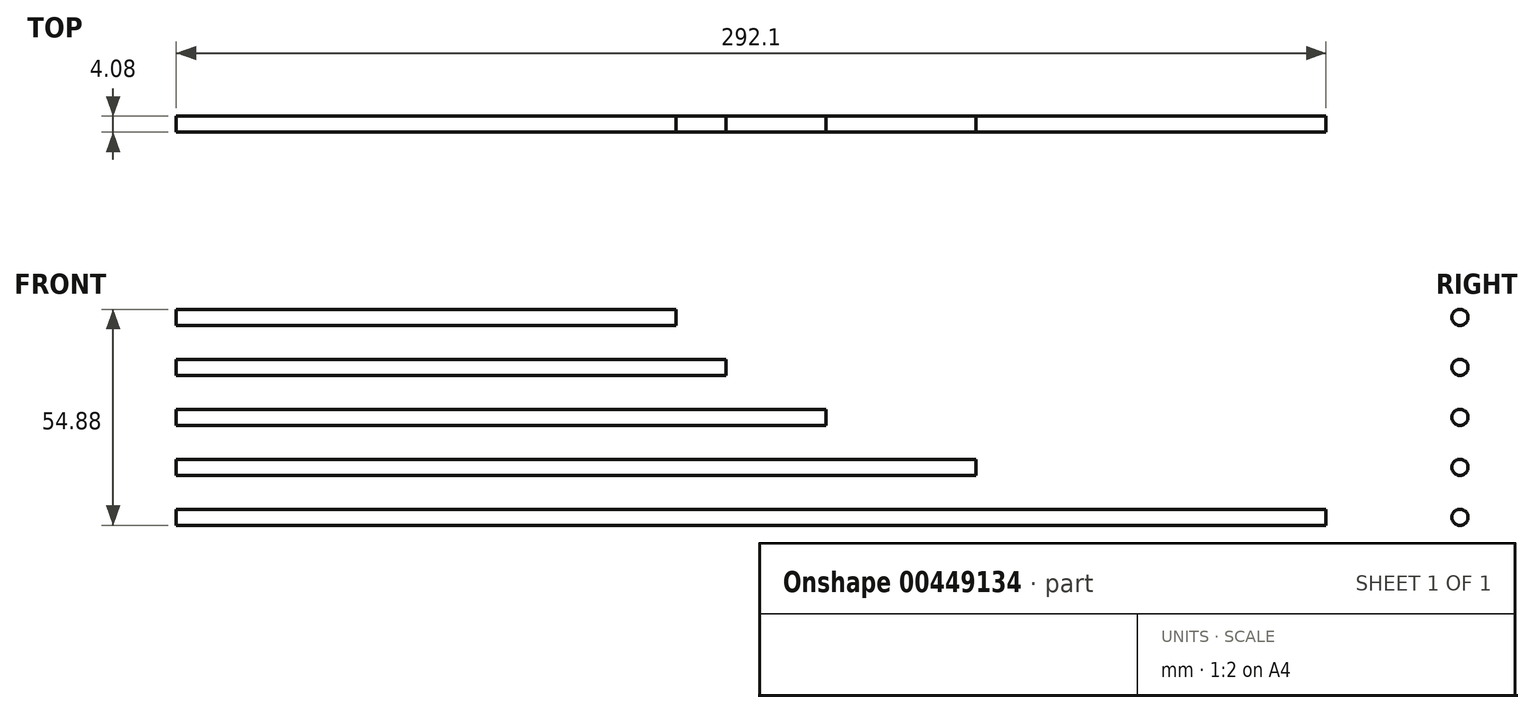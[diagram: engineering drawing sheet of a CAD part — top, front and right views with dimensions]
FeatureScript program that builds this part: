
annotation { "Feature Type Name" : "Feature", "Feature Type Description" : "" }
export const myFeature = defineFeature(function(context is Context, id is Id, definition is map)
    precondition{}
    {
        {
            var Q0;
            Q0=qCreatedBy(makeId("Right.planeOp"),FACE);
            var sketch = newSketch(context, id + "F0", { "sketchPlane" : qUnion([Q0])});
            skCircle(sketch, "E0", {"center": v(0, 0) * mm, "radius": 2.04 * mm});
            skSolve(sketch);
        }
        {
            var Q0;
            Q0=makeQuery(id+"F0.imprint","IMPRINT",FACE,{"disambiguationData":[TD([[makeQuery(id+"F0.imprint","IMPRINT",EDGE,{"derivedFrom":sQuery(id+"F0.wireOp",EDGE,"E0")}),1.0]])]});
            var Q1;
            Q1=sQuery(id+"F0.wireOp",EDGE,"E0");
            extrude(context, id + "F1", {"entities" : qUnion([Q0]), "surfaceEntities" : qUnion([Q1]), "depth" : 292.1 * mm});
        }
        {
            var Q0;
            Q0 = qSketchRegion(id + "F0", true);
            extrude(context, id + "F2", {"entities" : qUnion([Q0]), "depth" : 203.2 * mm});
        }
        {
            var Q0;
            Q0=makeQuery(id+"F1.opExtrude","SWEPT_BODY",BODY,{"disambiguationData":[OSD([sQuery(id+"F0.wireOp",EDGE,"E0")])]});
            var Q1;
            Q1=qCreatedBy(makeId("Top.planeOp"),FACE);
            transform(context, id + "F3", {"entities" : qUnion([Q0]), "transformType" : TransformType.TRANSLATION_DISTANCE, "transformDirection" : qUnion([Q1]), "distance" : 12.7 * mm, "makeCopy" : false});
        }
        {
            var Q0;
            Q0 = qSketchRegion(id + "F0", true);
            extrude(context, id + "F4", {"entities" : qUnion([Q0]), "depth" : 165.1 * mm});
        }
        {
            var Q0;
            Q0=makeQuery(id+"F2.opExtrude","SWEPT_BODY",BODY,{"disambiguationData":[OSD([sQuery(id+"F0.wireOp",EDGE,"E0")])]});
            var Q1;
            Q1=qCreatedBy(makeId("Top.planeOp"),FACE);
            transform(context, id + "F5", {"entities" : qUnion([Q0]), "transformType" : TransformType.TRANSLATION_DISTANCE, "transformDirection" : qUnion([Q1]), "distance" : 25.4 * mm, "makeCopy" : false});
        }
        {
            var Q0;
            Q0=makeQuery(id+"F4.opExtrude","SWEPT_BODY",BODY,{"disambiguationData":[OSD([sQuery(id+"F0.wireOp",EDGE,"E0")])]});
            var Q1;
            Q1=qCreatedBy(makeId("Top.planeOp"),FACE);
            transform(context, id + "F6", {"entities" : qUnion([Q0]), "transformType" : TransformType.TRANSLATION_DISTANCE, "transformDirection" : qUnion([Q1]), "distance" : 38.1 * mm, "makeCopy" : false});
        }
        {
            var Q0;
            Q0=makeQuery(id+"F0.imprint","IMPRINT",FACE,{"disambiguationData":[TD([[makeQuery(id+"F0.imprint","IMPRINT",EDGE,{"derivedFrom":sQuery(id+"F0.wireOp",EDGE,"E0")}),1.0]])]});
            extrude(context, id + "F7", {"entities" : qUnion([Q0]), "depth" : 139.7 * mm});
        }
        {
            var Q0;
            Q0=makeQuery(id+"F7.opExtrude","SWEPT_BODY",BODY,{"disambiguationData":[OSD([sQuery(id+"F0.wireOp",EDGE,"E0")])]});
            var Q1;
            Q1=qCreatedBy(makeId("Top.planeOp"),FACE);
            transform(context, id + "F8", {"entities" : qUnion([Q0]), "transformType" : TransformType.TRANSLATION_DISTANCE, "transformDirection" : qUnion([Q1]), "distance" : 50.8 * mm, "makeCopy" : false});
        }
        {
            var Q0;
            Q0=makeQuery(id+"F0.imprint","IMPRINT",FACE,{"disambiguationData":[TD([[makeQuery(id+"F0.imprint","IMPRINT",EDGE,{"derivedFrom":sQuery(id+"F0.wireOp",EDGE,"E0")}),1.0]])]});
            extrude(context, id + "F9", {"entities" : qUnion([Q0]), "depth" : 127 * mm});
        }
        {
            var Q0;
            Q0=makeQuery(id+"F9.opExtrude","SWEPT_BODY",BODY,{"disambiguationData":[OSD([sQuery(id+"F0.wireOp",EDGE,"E0")])]});
            var Q1;
            Q1=qCreatedBy(makeId("Top.planeOp"),FACE);
            transform(context, id + "F10", {"entities" : qUnion([Q0]), "transformType" : TransformType.TRANSLATION_DISTANCE, "transformDirection" : qUnion([Q1]), "distance" : 63.5 * mm, "makeCopy" : false});
        }
    });
